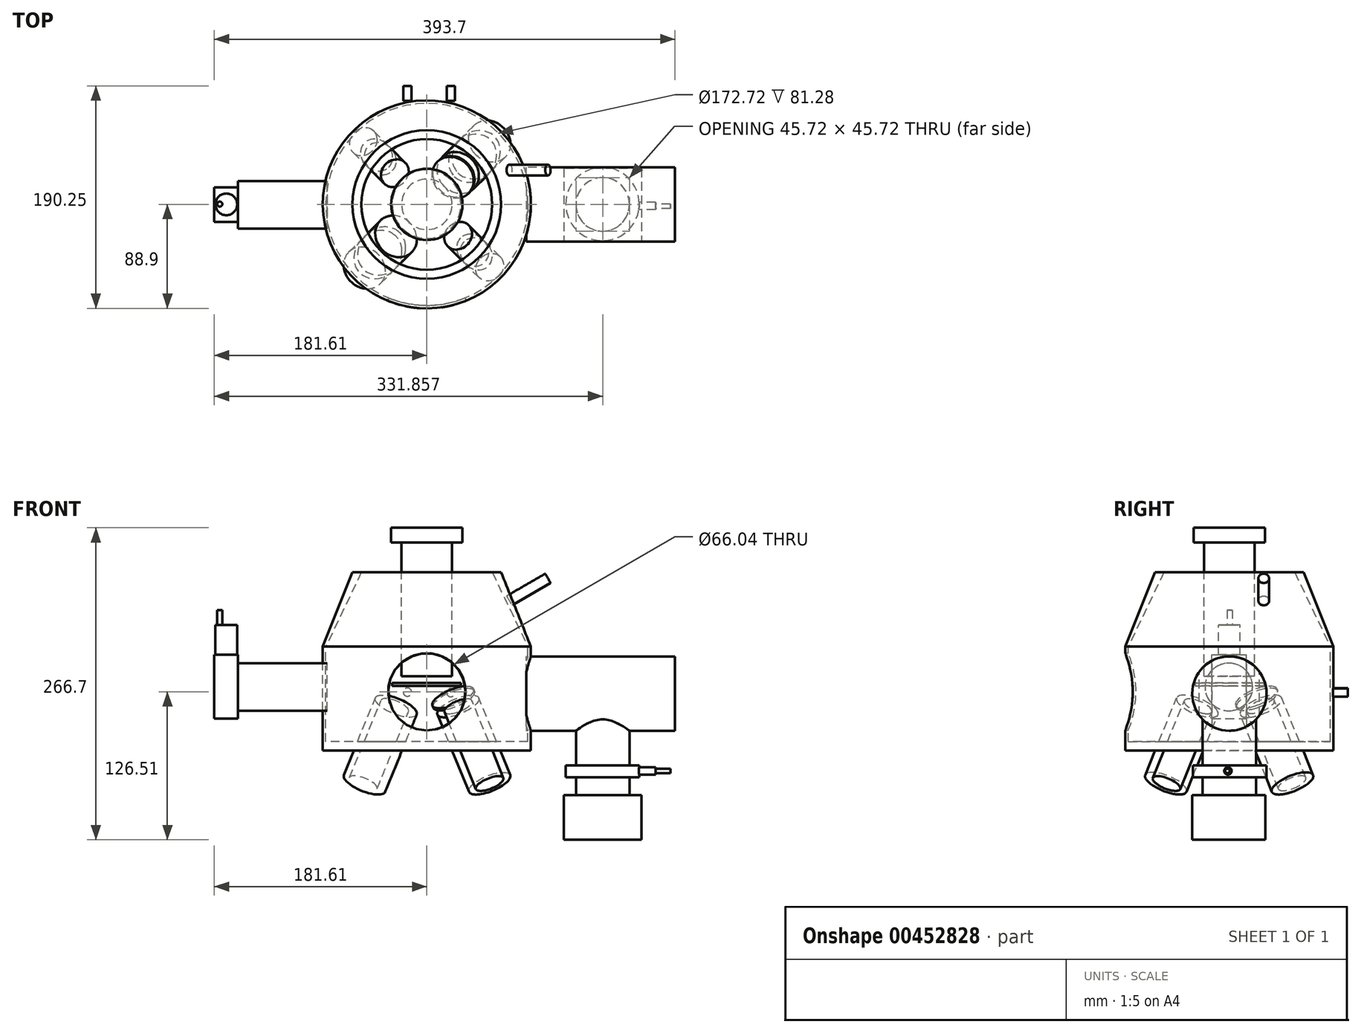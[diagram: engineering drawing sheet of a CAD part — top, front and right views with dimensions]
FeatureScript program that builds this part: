
annotation { "Feature Type Name" : "Feature", "Feature Type Description" : "" }
export const myFeature = defineFeature(function(context is Context, id is Id, definition is map)
    precondition{}
    {
        {
            var Q0;
            Q0=qCreatedBy(makeId("Top.planeOp"),FACE);
            var sketch = newSketch(context, id + "F0", { "sketchPlane" : qUnion([Q0])});
            skCircle(sketch, "E0", {"center": v(0, 0) * mm, "radius": 88.9 * mm});
            skSolve(sketch);
        }
        {
            var Q0;
            Q0=makeQuery(id+"F0.imprint","IMPRINT",FACE,{"disambiguationData":[TD([[makeQuery(id+"F0.imprint","IMPRINT",EDGE,{"derivedFrom":sQuery(id+"F0.wireOp",EDGE,"E0")}),1.0]])]});
            extrude(context, id + "F1", {"entities" : qUnion([Q0]), "oppositeDirection" : true, "depth" : 88.9 * mm});
        }
        {
            var Q0;
            Q0=makeQuery(id+"F1.opExtrude","CAP_FACE",FACE,{"disambiguationData":[OSD([sQuery(id+"F0.wireOp",EDGE,"E0")])],"isStart":true});
            var sketch = newSketch(context, id + "F2", { "sketchPlane" : qUnion([Q0])});
            skCircle(sketch, "E1", {"center": v(0, 0) * mm, "radius": 86.36 * mm});
            skSolve(sketch);
        }
        {
            var Q0;
            Q0=makeQuery(id+"F2.imprint","IMPRINT",FACE,{"disambiguationData":[TD([[makeQuery(id+"F2.imprint","IMPRINT",EDGE,{"derivedFrom":sQuery(id+"F2.wireOp",EDGE,"E1")}),1.0]])]});
            extrude(context, id + "F3", {"entities" : qUnion([Q0]), "operationType" : NewBodyOperationType.REMOVE, "oppositeDirection" : true, "depth" : 81.28 * mm});
        }
        {
            var Q0;
            Q0=qCreatedBy(makeId("Top.planeOp"),FACE);
            cPlane(context, id + "F4", {"entities" : qUnion([Q0]), "cplaneType" : CPlaneType.OFFSET, "offset" : 50.8 * mm, "oppositeDirection" : true, "width" : 152.4 * mm, "height" : 152.4 * mm});
        }
        {
            var Q0;
            Q0=qCreatedBy(id+"F4.planeOp",FACE);
            var sketch = newSketch(context, id + "F5", { "sketchPlane" : qUnion([Q0])});
            skCircle(sketch, "E2.cCircle", {"center": v(0, 0) * mm, "radius": 53.88 * mm, "construction": true});
            skLineSegment(sketch, "E2.0", {"start": v(0, -53.88) * mm, "end": v(-53.88, 0) * mm});
            skLineSegment(sketch, "E2.1", {"start": v(-53.88, 0) * mm, "end": v(0, 53.88) * mm});
            skLineSegment(sketch, "E2.2", {"start": v(0, 53.88) * mm, "end": v(53.88, 0) * mm});
            skLineSegment(sketch, "E2.3", {"start": v(53.88, 0) * mm, "end": v(0, -53.88) * mm});
            skPoint(sketch, "E3", {"position": v(-26.94, 26.94) * mm});
            skPoint(sketch, "E4", {"position": v(26.94, 26.94) * mm});
            skPoint(sketch, "E5", {"position": v(26.94, -26.94) * mm});
            skPoint(sketch, "E6", {"position": v(-26.94, -26.94) * mm});
            skSolve(sketch);
        }
        {
            var Q0;
            Q0=sQuery(id+"F5.wireOp",EDGE,"E2.1");
            cPlane(context, id + "F6", {"entities" : qUnion([Q0]), "cplaneType" : CPlaneType.LINE_ANGLE, "offset" : 25.4 * mm, "angle" : 30 * degree, "width" : 152.4 * mm, "height" : 152.4 * mm});
        }
        {
            var Q0;
            Q0=qCreatedBy(id+"F6.planeOp",FACE);
            var sketch = newSketch(context, id + "F7", { "sketchPlane" : qUnion([Q0])});
            skCircle(sketch, "E7", {"center": v(-5.44, 5.5) * mm, "radius": 12.7 * mm});
            skSolve(sketch);
        }
        {
            var Q0;
            Q0 = qSketchRegion(id + "F7", true);
            extrude(context, id + "F8", {"entities" : qUnion([Q0]), "operationType" : NewBodyOperationType.ADD, "oppositeDirection" : true, "depth" : 76.2 * mm});
        }
        {
            var Q0;
            Q0=sQuery(id+"F5.wireOp",EDGE,"E2.0");
            cPlane(context, id + "F9", {"entities" : qUnion([Q0]), "cplaneType" : CPlaneType.LINE_ANGLE, "offset" : 25.4 * mm, "angle" : 30 * degree, "width" : 152.4 * mm, "height" : 152.4 * mm});
        }
        {
            var Q0;
            Q0=qCreatedBy(id+"F9.planeOp",FACE);
            var sketch = newSketch(context, id + "F10", { "sketchPlane" : qUnion([Q0])});
            skCircle(sketch, "E8", {"center": v(-4.32, -6.08) * mm, "radius": 19.05 * mm});
            skSolve(sketch);
        }
        {
            var Q0;
            Q0 = qSketchRegion(id + "F10", true);
            extrude(context, id + "F11", {"entities" : qUnion([Q0]), "operationType" : NewBodyOperationType.ADD, "oppositeDirection" : true, "depth" : 76.2 * mm});
        }
        {
            var Q0;
            Q0=sQuery(id+"F5.wireOp",EDGE,"E2.3");
            cPlane(context, id + "F12", {"entities" : qUnion([Q0]), "cplaneType" : CPlaneType.LINE_ANGLE, "offset" : 25.4 * mm, "angle" : 30 * degree, "width" : 152.4 * mm, "height" : 152.4 * mm});
        }
        {
            var Q0;
            Q0=qCreatedBy(id+"F12.planeOp",FACE);
            var sketch = newSketch(context, id + "F13", { "sketchPlane" : qUnion([Q0])});
            skCircle(sketch, "E9", {"center": v(4.76, 5.52) * mm, "radius": 12.7 * mm});
            skSolve(sketch);
        }
        {
            var Q0;
            Q0 = qSketchRegion(id + "F13", true);
            extrude(context, id + "F14", {"entities" : qUnion([Q0]), "operationType" : NewBodyOperationType.ADD, "depth" : 76.2 * mm});
        }
        {
            var Q0;
            Q0=sQuery(id+"F5.wireOp",EDGE,"E2.2");
            cPlane(context, id + "F15", {"entities" : qUnion([Q0]), "cplaneType" : CPlaneType.LINE_ANGLE, "offset" : 25.4 * mm, "angle" : 30 * degree, "width" : 152.4 * mm, "height" : 152.4 * mm});
        }
        {
            var Q0;
            Q0=qCreatedBy(id+"F15.planeOp",FACE);
            var sketch = newSketch(context, id + "F16", { "sketchPlane" : qUnion([Q0])});
            skCircle(sketch, "E10", {"center": v(4.67, -5.76) * mm, "radius": 19.05 * mm});
            skSolve(sketch);
        }
        {
            var Q0;
            Q0 = qSketchRegion(id + "F16", true);
            extrude(context, id + "F17", {"entities" : qUnion([Q0]), "operationType" : NewBodyOperationType.ADD, "depth" : 76.2 * mm});
        }
        {
            var Q0;
            Q0=qCreatedBy(makeId("Top.planeOp"),FACE);
            cPlane(context, id + "F18", {"entities" : qUnion([Q0]), "cplaneType" : CPlaneType.OFFSET, "offset" : 88.9 * mm, "width" : 152.4 * mm, "height" : 152.4 * mm});
        }
        {
            var Q0;
            Q0=qCreatedBy(id+"F18.planeOp",FACE);
            var sketch = newSketch(context, id + "F19", { "sketchPlane" : qUnion([Q0])});
            skCircle(sketch, "E11", {"center": v(0, 0) * mm, "radius": 21.59 * mm});
            skSolve(sketch);
        }
        {
            var Q0;
            Q0=makeQuery(id+"F19.imprint","IMPRINT",FACE,{"disambiguationData":[TD([[makeQuery(id+"F19.imprint","IMPRINT",EDGE,{"derivedFrom":sQuery(id+"F19.wireOp",EDGE,"E11")}),1.0]])]});
            extrude(context, id + "F20", {"entities" : qUnion([Q0]), "oppositeDirection" : true, "depth" : 114.3 * mm});
        }
        {
            var Q0;
            Q0=qCreatedBy(id+"F18.planeOp",FACE);
            var sketch = newSketch(context, id + "F21", { "sketchPlane" : qUnion([Q0])});
            skCircle(sketch, "E12", {"center": v(0, 0) * mm, "radius": 30.48 * mm});
            skSolve(sketch);
        }
        {
            var Q0;
            Q0 = qSketchRegion(id + "F21", true);
            extrude(context, id + "F22", {"entities" : qUnion([Q0]), "operationType" : NewBodyOperationType.ADD, "depth" : 12.7 * mm});
        }
        {
            var Q0;
            Q0=qCreatedBy(id+"F18.planeOp",FACE);
            cPlane(context, id + "F23", {"entities" : qUnion([Q0]), "cplaneType" : CPlaneType.OFFSET, "offset" : 25.4 * mm, "oppositeDirection" : true, "width" : 152.4 * mm, "height" : 152.4 * mm});
        }
        {
            var Q0;
            Q0=qCreatedBy(id+"F23.planeOp",FACE);
            var sketch = newSketch(context, id + "F24", { "sketchPlane" : qUnion([Q0])});
            skCircle(sketch, "E13", {"center": v(0, 0) * mm, "radius": 63.5 * mm});
            skSolve(sketch);
        }
        {
            var Q0;
            Q0=qCreatedBy(id+"F23.planeOp",FACE);
            var sketch = newSketch(context, id + "F25", { "sketchPlane" : qUnion([Q0])});
            skCircle(sketch, "E14", {"center": v(0, 0) * mm, "radius": 55.88 * mm});
            skSolve(sketch);
        }
        {
            var Q0;
            Q0 = qSketchRegion(id + "F24", true);
            var Q1;
            Q1 = qSketchRegion(id + "F0", true);
            loft(context, id + "F26", {"sheetProfilesArray" : [{ "sheetProfileEntities" : qUnion([Q0]) }, { "sheetProfileEntities" : qUnion([Q1]) }]});
        }
        {
            var Q0;
            Q0 = qSketchRegion(id + "F25", true);
            var Q1;
            Q1 = qSketchRegion(id + "F2", true);
            loft(context, id + "F27", {"operationType" : NewBodyOperationType.REMOVE, "sheetProfilesArray" : [{ "sheetProfileEntities" : qUnion([Q0]) }, { "sheetProfileEntities" : qUnion([Q1]) }]});
        }
        {
            var Q0;
            Q0 = qSketchRegion(id + "F19", true);
            var Q1;
            Q1=makeQuery(id+"F27.boolean.opBoolean","COPY",FACE,{"derivedFrom":makeQuery(id+"F27.opLoft","CAP_FACE",FACE,{"disambiguationData":[OSD([makeQuery(id+"F2.imprint","IMPRINT",FACE,{"disambiguationData":[TD([[makeQuery(id+"F2.imprint","IMPRINT",EDGE,{"derivedFrom":sQuery(id+"F2.wireOp",EDGE,"E1")}),1.0]])]})])],"isStart":true})});
            loft(context, id + "F28", {"sheetProfilesArray" : [{ "sheetProfileEntities" : qUnion([Q0]) }, { "sheetProfileEntities" : qUnion([Q1]) }]});
        }
        {
            var Q0;
            Q0=qCreatedBy(makeId("Right.planeOp"),FACE);
            cPlane(context, id + "F29", {"entities" : qUnion([Q0]), "cplaneType" : CPlaneType.OFFSET, "offset" : 85.1 * mm, "oppositeDirection" : true, "width" : 152.4 * mm, "height" : 152.4 * mm});
        }
        {
            var Q0;
            Q0=qCreatedBy(id+"F29.planeOp",FACE);
            var sketch = newSketch(context, id + "F30", { "sketchPlane" : qUnion([Q0])});
            skCircle(sketch, "E15", {"center": v(-0.45, -34.45) * mm, "radius": 20.32 * mm});
            skSolve(sketch);
        }
        {
            var Q0;
            Q0 = qSketchRegion(id + "F30", true);
            extrude(context, id + "F31", {"entities" : qUnion([Q0]), "oppositeDirection" : true, "depth" : 76.2 * mm});
        }
        {
            var Q0;
            Q0=qCreatedBy(makeId("Right.planeOp"),FACE);
            cPlane(context, id + "F32", {"entities" : qUnion([Q0]), "cplaneType" : CPlaneType.OFFSET, "offset" : 85.1 * mm, "width" : 152.4 * mm, "height" : 152.4 * mm});
        }
        {
            var Q0;
            Q0=qCreatedBy(id+"F32.planeOp",FACE);
            var sketch = newSketch(context, id + "F33", { "sketchPlane" : qUnion([Q0])});
            skCircle(sketch, "E16", {"center": v(0, -40.07) * mm, "radius": 31.75 * mm});
            skSolve(sketch);
        }
        {
            var Q0;
            Q0 = qSketchRegion(id + "F33", true);
            extrude(context, id + "F34", {"entities" : qUnion([Q0]), "operationType" : NewBodyOperationType.ADD, "depth" : 127 * mm});
        }
        {
            var Q0;
            Q0=qCreatedBy(id+"F4.planeOp",FACE);
            var sketch = newSketch(context, id + "F35", { "sketchPlane" : qUnion([Q0])});
            skCircle(sketch, "E17", {"center": v(150.25, 0) * mm, "radius": 22.86 * mm});
            skSolve(sketch);
        }
        {
            var Q0;
            Q0 = qSketchRegion(id + "F35", true);
            extrude(context, id + "F36", {"entities" : qUnion([Q0]), "operationType" : NewBodyOperationType.ADD, "oppositeDirection" : true, "depth" : 76.2 * mm});
        }
        {
            var Q0;
            Q0=qCreatedBy(makeId("Front.planeOp"),FACE);
            cPlane(context, id + "F37", {"entities" : qUnion([Q0]), "cplaneType" : CPlaneType.OFFSET, "offset" : 88.9 * mm, "width" : 152.4 * mm, "height" : 152.4 * mm});
        }
        {
            var Q0;
            Q0=qCreatedBy(id+"F37.planeOp",FACE);
            var sketch = newSketch(context, id + "F38", { "sketchPlane" : qUnion([Q0])});
            skCircle(sketch, "E18", {"center": v(0, -38.59) * mm, "radius": 33.02 * mm});
            skSolve(sketch);
        }
        {
            var Q0;
            Q0 = qSketchRegion(id + "F38", true);
            extrude(context, id + "F39", {"entities" : qUnion([Q0]), "operationType" : NewBodyOperationType.REMOVE, "oppositeDirection" : true, "depth" : 12.7 * mm});
        }
        {
            var Q0;
            Q0=qCreatedBy(makeId("Front.planeOp"),FACE);
            cPlane(context, id + "F40", {"entities" : qUnion([Q0]), "cplaneType" : CPlaneType.OFFSET, "offset" : 88.65 * mm, "oppositeDirection" : true, "width" : 152.4 * mm, "height" : 152.4 * mm});
        }
        {
            var Q0;
            Q0=qCreatedBy(id+"F40.planeOp",FACE);
            var sketch = newSketch(context, id + "F41", { "sketchPlane" : qUnion([Q0])});
            skCircle(sketch, "E19", {"center": v(20.44, -39.28) * mm, "radius": 3.56 * mm});
            skSolve(sketch);
        }
        {
            var Q0;
            Q0=qCreatedBy(id+"F40.planeOp",FACE);
            var sketch = newSketch(context, id + "F42", { "sketchPlane" : qUnion([Q0])});
            skCircle(sketch, "E20", {"center": v(-16.65, -38.83) * mm, "radius": 3.56 * mm});
            skSolve(sketch);
        }
        {
            var Q0;
            Q0 = qSketchRegion(id + "F41", true);
            extrude(context, id + "F43", {"entities" : qUnion([Q0]), "oppositeDirection" : true, "depth" : 12.7 * mm});
        }
        {
            var Q0;
            Q0 = qSketchRegion(id + "F42", true);
            extrude(context, id + "F44", {"entities" : qUnion([Q0]), "oppositeDirection" : true, "depth" : 12.7 * mm});
        }
        {
            var Q0;
            Q0=qCreatedBy(makeId("Top.planeOp"),FACE);
            cPlane(context, id + "F45", {"entities" : qUnion([Q0]), "cplaneType" : CPlaneType.OFFSET, "offset" : 38.6 * mm, "oppositeDirection" : true, "width" : 152.4 * mm, "height" : 152.4 * mm});
        }
        {
            var Q0;
            Q0=makeQuery(id+"F36.opExtrude","CAP_FACE",FACE,{"disambiguationData":[OSD([sQuery(id+"F35.wireOp",EDGE,"E17")])],"isStart":false});
            cPlane(context, id + "F46", {"entities" : qUnion([Q0]), "cplaneType" : CPlaneType.OFFSET, "offset" : 25.4 * mm, "oppositeDirection" : true, "width" : 152.4 * mm, "height" : 152.4 * mm});
        }
        {
            var Q0;
            Q0=qCreatedBy(id+"F46.planeOp",FACE);
            var sketch = newSketch(context, id + "F47", { "sketchPlane" : qUnion([Q0])});
            skCircle(sketch, "E21", {"center": v(150.11, -0.34) * mm, "radius": 31.35 * mm});
            skSolve(sketch);
        }
        {
            var Q0;
            Q0 = qSketchRegion(id + "F47", true);
            extrude(context, id + "F48", {"entities" : qUnion([Q0]), "operationType" : NewBodyOperationType.ADD, "depth" : 10.16 * mm});
        }
        {
            var Q0;
            Q0=qCreatedBy(makeId("Right.planeOp"),FACE);
            cPlane(context, id + "F49", {"entities" : qUnion([Q0]), "cplaneType" : CPlaneType.OFFSET, "offset" : 177.55 * mm, "width" : 152.4 * mm, "height" : 152.4 * mm});
        }
        {
            var Q0;
            Q0=qCreatedBy(id+"F49.planeOp",FACE);
            var sketch = newSketch(context, id + "F50", { "sketchPlane" : qUnion([Q0])});
            skCircle(sketch, "E22", {"center": v(-1.2, -106.18) * mm, "radius": 3.17 * mm});
            skSolve(sketch);
        }
        {
            var Q0;
            Q0 = qSketchRegion(id + "F50", true);
            extrude(context, id + "F51", {"entities" : qUnion([Q0]), "operationType" : NewBodyOperationType.ADD, "depth" : 17.78 * mm});
        }
        {
            var Q0;
            Q0=qCreatedBy(id+"F49.planeOp",FACE);
            var sketch = newSketch(context, id + "F52", { "sketchPlane" : qUnion([Q0])});
            skCircle(sketch, "E23", {"center": v(-1.65, -106.18) * mm, "radius": 1.9 * mm});
            skSolve(sketch);
        }
        {
            var Q0;
            Q0 = qSketchRegion(id + "F52", true);
            extrude(context, id + "F53", {"entities" : qUnion([Q0]), "operationType" : NewBodyOperationType.ADD, "depth" : 30.48 * mm});
        }
        {
            var Q0;
            Q0=qCreatedBy(makeId("Top.planeOp"),FACE);
            cPlane(context, id + "F54", {"entities" : qUnion([Q0]), "cplaneType" : CPlaneType.OFFSET, "offset" : 33.53 * mm, "oppositeDirection" : true, "width" : 152.4 * mm, "height" : 152.4 * mm});
        }
        {
            var Q0;
            Q0=qCreatedBy(id+"F54.planeOp",FACE);
            var sketch = newSketch(context, id + "F55", { "sketchPlane" : qUnion([Q0])});
            skCircle(sketch, "E24", {"center": v(-0.3, 0.22) * mm, "radius": 29.31 * mm});
            skSolve(sketch);
        }
        {
            var Q0;
            Q0 = qSketchRegion(id + "F55", true);
            extrude(context, id + "F56", {"entities" : qUnion([Q0]), "depth" : 2.54 * mm});
        }
        {
            var Q0;
            Q0=makeQuery(id+"F16.imprint","IMPRINT",FACE,{"disambiguationData":[TD([[makeQuery(id+"F16.imprint","IMPRINT",EDGE,{"derivedFrom":sQuery(id+"F16.wireOp",EDGE,"E10")}),1.0]])]});
            cPlane(context, id + "F57", {"entities" : qUnion([Q0]), "cplaneType" : CPlaneType.OFFSET, "offset" : 7.62 * mm, "oppositeDirection" : true, "width" : 152.4 * mm, "height" : 152.4 * mm});
        }
        {
            var Q0;
            Q0=qCreatedBy(id+"F57.planeOp",FACE);
            var sketch = newSketch(context, id + "F58", { "sketchPlane" : qUnion([Q0])});
            skCircle(sketch, "E25", {"center": v(3.65, -4.9) * mm, "radius": 18.97 * mm});
            skSolve(sketch);
        }
        {
            var Q0;
            Q0 = qSketchRegion(id + "F58", true);
            extrude(context, id + "F59", {"entities" : qUnion([Q0]), "oppositeDirection" : true, "depth" : 2.03 * mm});
        }
        {
            var Q0;
            Q0=makeQuery(id+"F36.opExtrude","CAP_FACE",FACE,{"disambiguationData":[OSD([sQuery(id+"F35.wireOp",EDGE,"E17")])],"isStart":false});
            cPlane(context, id + "F60", {"entities" : qUnion([Q0]), "cplaneType" : CPlaneType.OFFSET, "offset" : 38.1 * mm, "width" : 152.4 * mm, "height" : 152.4 * mm});
        }
        {
            var Q0;
            Q0=qCreatedBy(id+"F60.planeOp",FACE);
            var sketch = newSketch(context, id + "F61", { "sketchPlane" : qUnion([Q0])});
            skLineSegment(sketch, "E26.bottom", {"start": v(183.28, -30.72) * mm, "end": v(117.04, -30.72) * mm});
            skLineSegment(sketch, "E26.top", {"start": v(183.28, 31.76) * mm, "end": v(117.04, 31.76) * mm});
            skLineSegment(sketch, "E26.left", {"start": v(183.28, -30.72) * mm, "end": v(183.28, 31.76) * mm});
            skLineSegment(sketch, "E26.right", {"start": v(117.04, -30.72) * mm, "end": v(117.04, 31.76) * mm});
            skPoint(sketch, "E26.middle", {"position": v(150.16, 0.52) * mm});
            skSolve(sketch);
        }
        {
            var Q0;
            Q0=makeQuery(id+"F61.imprint","IMPRINT",FACE,{"disambiguationData":[TD([[makeQuery(id+"F61.imprint","IMPRINT",EDGE,{"derivedFrom":sQuery(id+"F61.wireOp",EDGE,"E26.bottom")}),-1.0]])]});
            extrude(context, id + "F62", {"entities" : qUnion([Q0]), "operationType" : NewBodyOperationType.ADD, "oppositeDirection" : true, "depth" : 38.1 * mm, "offsetDistance" : 25.4 * mm});
        }
        {
            var Q0;
            Q0=makeQuery(id+"F31.opExtrude","CAP_FACE",FACE,{"disambiguationData":[OSD([sQuery(id+"F30.wireOp",EDGE,"E15")])],"isStart":false});
            cPlane(context, id + "F63", {"entities" : qUnion([Q0]), "cplaneType" : CPlaneType.OFFSET, "offset" : 20.32 * mm, "width" : 152.4 * mm, "height" : 152.4 * mm});
        }
        {
            var Q0;
            Q0=qCreatedBy(id+"F63.planeOp",FACE);
            var sketch = newSketch(context, id + "F64", { "sketchPlane" : qUnion([Q0])});
            skLineSegment(sketch, "E27.bottom", {"start": v(14.88, -61.5) * mm, "end": v(-14.6, -61.5) * mm});
            skLineSegment(sketch, "E27.top", {"start": v(14.88, -6.75) * mm, "end": v(-14.6, -6.75) * mm});
            skLineSegment(sketch, "E27.left", {"start": v(14.88, -61.5) * mm, "end": v(14.88, -6.75) * mm});
            skLineSegment(sketch, "E27.right", {"start": v(-14.6, -61.5) * mm, "end": v(-14.6, -6.75) * mm});
            skPoint(sketch, "E27.middle", {"position": v(0.14, -34.12) * mm});
            skSolve(sketch);
        }
        {
            var Q0;
            Q0 = qSketchRegion(id + "F64", true);
            extrude(context, id + "F65", {"entities" : qUnion([Q0]), "operationType" : NewBodyOperationType.ADD, "oppositeDirection" : true, "depth" : 20.32 * mm, "offsetDistance" : 25.4 * mm});
        }
        {
            var Q0;
            Q0=makeQuery(id+"F65.opExtrude","SWEPT_FACE",FACE,{"disambiguationData":[OSD([sQuery(id+"F64.wireOp",EDGE,"E27.top")])]});
            cPlane(context, id + "F66", {"entities" : qUnion([Q0]), "cplaneType" : CPlaneType.OFFSET, "offset" : 25.4 * mm, "width" : 152.4 * mm, "height" : 152.4 * mm});
        }
        {
            var Q0;
            Q0=qCreatedBy(id+"F66.planeOp",FACE);
            var sketch = newSketch(context, id + "F67", { "sketchPlane" : qUnion([Q0])});
            skCircle(sketch, "E28", {"center": v(-171.36, 0.06) * mm, "radius": 9.29 * mm});
            skSolve(sketch);
        }
        {
            var Q0;
            Q0 = qSketchRegion(id + "F67", true);
            extrude(context, id + "F68", {"entities" : qUnion([Q0]), "oppositeDirection" : true, "depth" : 25.4 * mm, "offsetDistance" : 25.4 * mm});
        }
        {
            var Q0;
            Q0=makeQuery(id+"F68.opExtrude","CAP_FACE",FACE,{"disambiguationData":[OSD([sQuery(id+"F67.wireOp",EDGE,"E28")])],"isStart":true});
            var sketch = newSketch(context, id + "F69", { "sketchPlane" : qUnion([Q0])});
            skCircle(sketch, "E29", {"center": v(-176.94, 0.24) * mm, "radius": 2.15 * mm});
            skSolve(sketch);
        }
        {
            var Q0;
            Q0 = qSketchRegion(id + "F69", true);
            extrude(context, id + "F70", {"entities" : qUnion([Q0]), "operationType" : NewBodyOperationType.ADD, "depth" : 12.7 * mm, "offsetDistance" : 25.4 * mm});
        }
        {
            var Q0;
            Q0=makeQuery(id+"F65.opExtrude","SWEPT_FACE",FACE,{"disambiguationData":[OSD([sQuery(id+"F64.wireOp",EDGE,"E27.top")])]});
            var Q1;
            Q1=makeQuery(id+"F65.opExtrude","CAP_EDGE",EDGE,{"disambiguationData":[OSD([sQuery(id+"F64.wireOp",EDGE,"E27.top")])],"isStart":true});
            cPlane(context, id + "F71", {"entities" : qUnion([Q0, Q1]), "cplaneType" : CPlaneType.LINE_ANGLE, "offset" : 25.4 * mm, "angle" : 60 * degree, "width" : 152.4 * mm, "height" : 152.4 * mm});
        }
        {
            var Q0;
            Q0=qCreatedBy(id+"F71.planeOp",FACE);
            cPlane(context, id + "F72", {"entities" : qUnion([Q0]), "cplaneType" : CPlaneType.OFFSET, "offset" : 241.3 * mm, "oppositeDirection" : true, "width" : 152.4 * mm, "height" : 152.4 * mm});
        }
        {
            var Q0;
            Q0=qCreatedBy(id+"F72.planeOp",FACE);
            var sketch = newSketch(context, id + "F73", { "sketchPlane" : qUnion([Q0])});
            skCircle(sketch, "E30", {"center": v(-29.38, -1.16) * mm, "radius": 4.6 * mm});
            skSolve(sketch);
        }
        {
            var Q0;
            Q0 = qSketchRegion(id + "F73", true);
            extrude(context, id + "F74", {"entities" : qUnion([Q0]), "oppositeDirection" : true, "depth" : 38.1 * mm, "offsetDistance" : 25.4 * mm});
        }
    });
